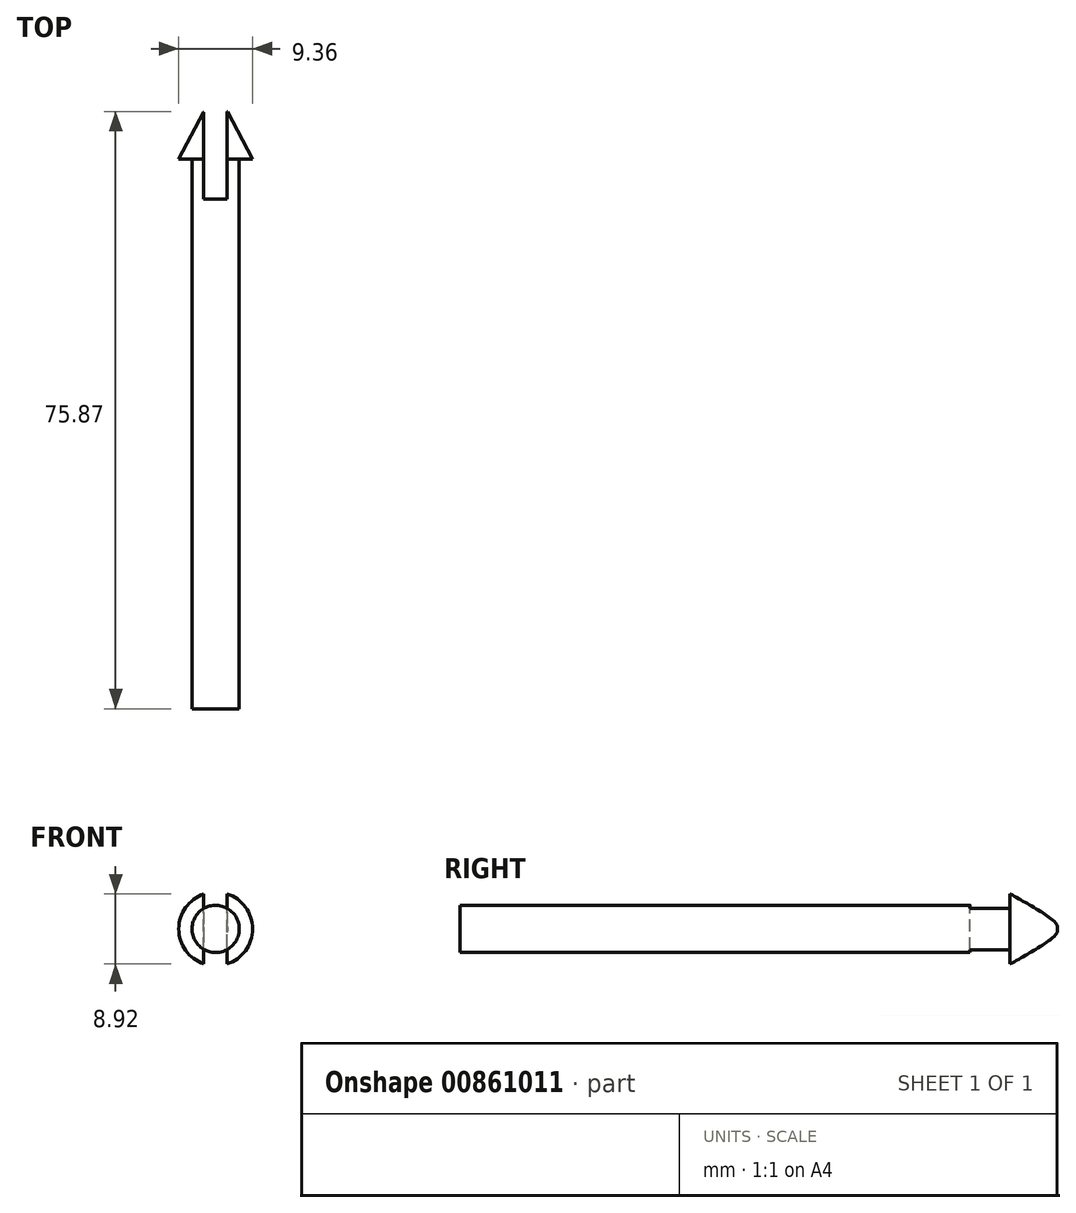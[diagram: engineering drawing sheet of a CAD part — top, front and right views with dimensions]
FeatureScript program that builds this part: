
annotation { "Feature Type Name" : "Feature", "Feature Type Description" : "" }
export const myFeature = defineFeature(function(context is Context, id is Id, definition is map)
    precondition{}
    {
        {
            var Q0;
            Q0=qCreatedBy(makeId("Front.planeOp"),FACE);
            var sketch = newSketch(context, id + "F0", { "sketchPlane" : qUnion([Q0])});
            skCircle(sketch, "E0", {"center": v(0, 0) * mm, "radius": 3 * mm});
            skSolve(sketch);
        }
        {
            var Q0;
            Q0=makeQuery(id+"F0.imprint","IMPRINT",FACE,{"disambiguationData":[TD([[makeQuery(id+"F0.imprint","IMPRINT",EDGE,{"derivedFrom":sQuery(id+"F0.wireOp",EDGE,"E0")}),1.0]])]});
            extrude(context, id + "F1", {"entities" : qUnion([Q0]), "depth" : 69.85 * mm, "offsetDistance" : 25 * mm});
        }
        {
            var Q0;
            Q0=qCreatedBy(makeId("Top.planeOp"),FACE);
            var sketch = newSketch(context, id + "F2", { "sketchPlane" : qUnion([Q0])});
            skLineSegment(sketch, "E1", {"start": v(0, 0) * mm, "end": v(0, 8.86) * mm});
            skLineSegment(sketch, "E2", {"start": v(0, 8.86) * mm, "end": v(-4.68, 0) * mm});
            skLineSegment(sketch, "E3", {"start": v(-4.68, 0) * mm, "end": v(0, 0) * mm});
            skSolve(sketch);
        }
        {
            var Q0;
            Q0=makeQuery(id+"F2.imprint","IMPRINT",FACE,{"disambiguationData":[TD([[makeQuery(id+"F2.imprint","IMPRINT",EDGE,{"derivedFrom":sQuery(id+"F2.wireOp",EDGE,"E1")}),1.0]])]});
            var Q1;
            Q1=sQuery(id+"F2.wireOp",EDGE,"E1");
            revolve(context, id + "F3", {"operationType" : NewBodyOperationType.ADD, "surfaceOperationType" : NewSurfaceOperationType.NEW, "entities" : qUnion([Q0]), "axis" : qUnion([Q1]), "revolveType" : RevolveType.FULL});
        }
        {
            var Q0;
            Q0=qCreatedBy(makeId("Top.planeOp"),FACE);
            var sketch = newSketch(context, id + "F4", { "sketchPlane" : qUnion([Q0])});
            skLineSegment(sketch, "E4", {"start": v(-1.5, 6.05) * mm, "end": v(-1.5, -5.07) * mm});
            skLineSegment(sketch, "E5", {"start": v(-1.5, -5.07) * mm, "end": v(1.43, -5.07) * mm});
            skLineSegment(sketch, "E6", {"start": v(1.43, -5.07) * mm, "end": v(1.43, 6.1) * mm});
            skLineSegment(sketch, "E7", {"start": v(-1.5, 6.05) * mm, "end": v(1.43, 6.1) * mm});
            skSolve(sketch);
        }
        {
            var Q0;
            Q0 = qSketchRegion(id + "F4", true);
            extrude(context, id + "F5", {"entities" : qUnion([Q0]), "operationType" : NewBodyOperationType.REMOVE, "oppositeDirection" : true, "depth" : 25 * mm, "offsetDistance" : 25 * mm});
        }
        {
            var Q0;
            Q0 = qSketchRegion(id + "F4", true);
            extrude(context, id + "F6", {"entities" : qUnion([Q0]), "operationType" : NewBodyOperationType.REMOVE, "depth" : 10.9 * mm, "offsetDistance" : 25 * mm});
        }
        {
            var Q0;
            Q0=qCreatedBy(makeId("Top.planeOp"),FACE);
            var sketch = newSketch(context, id + "F7", { "sketchPlane" : qUnion([Q0])});
            skLineSegment(sketch, "E8", {"start": v(-1.55, 5.98) * mm, "end": v(0, 8.9) * mm});
            skLineSegment(sketch, "E9", {"start": v(0, 8.9) * mm, "end": v(1.5, 6.02) * mm});
            skLineSegment(sketch, "E10", {"start": v(1.5, 6.02) * mm, "end": v(-1.55, 5.98) * mm});
            skSolve(sketch);
        }
        {
            var Q0;
            Q0 = qSketchRegion(id + "F7", true);
            extrude(context, id + "F8", {"entities" : qUnion([Q0]), "operationType" : NewBodyOperationType.REMOVE, "oppositeDirection" : true, "depth" : 25 * mm, "offsetDistance" : 25 * mm});
        }
        {
            var Q0;
            Q0 = qSketchRegion(id + "F7", true);
            extrude(context, id + "F9", {"entities" : qUnion([Q0]), "operationType" : NewBodyOperationType.REMOVE, "depth" : 25 * mm, "offsetDistance" : 25 * mm});
        }
    });
